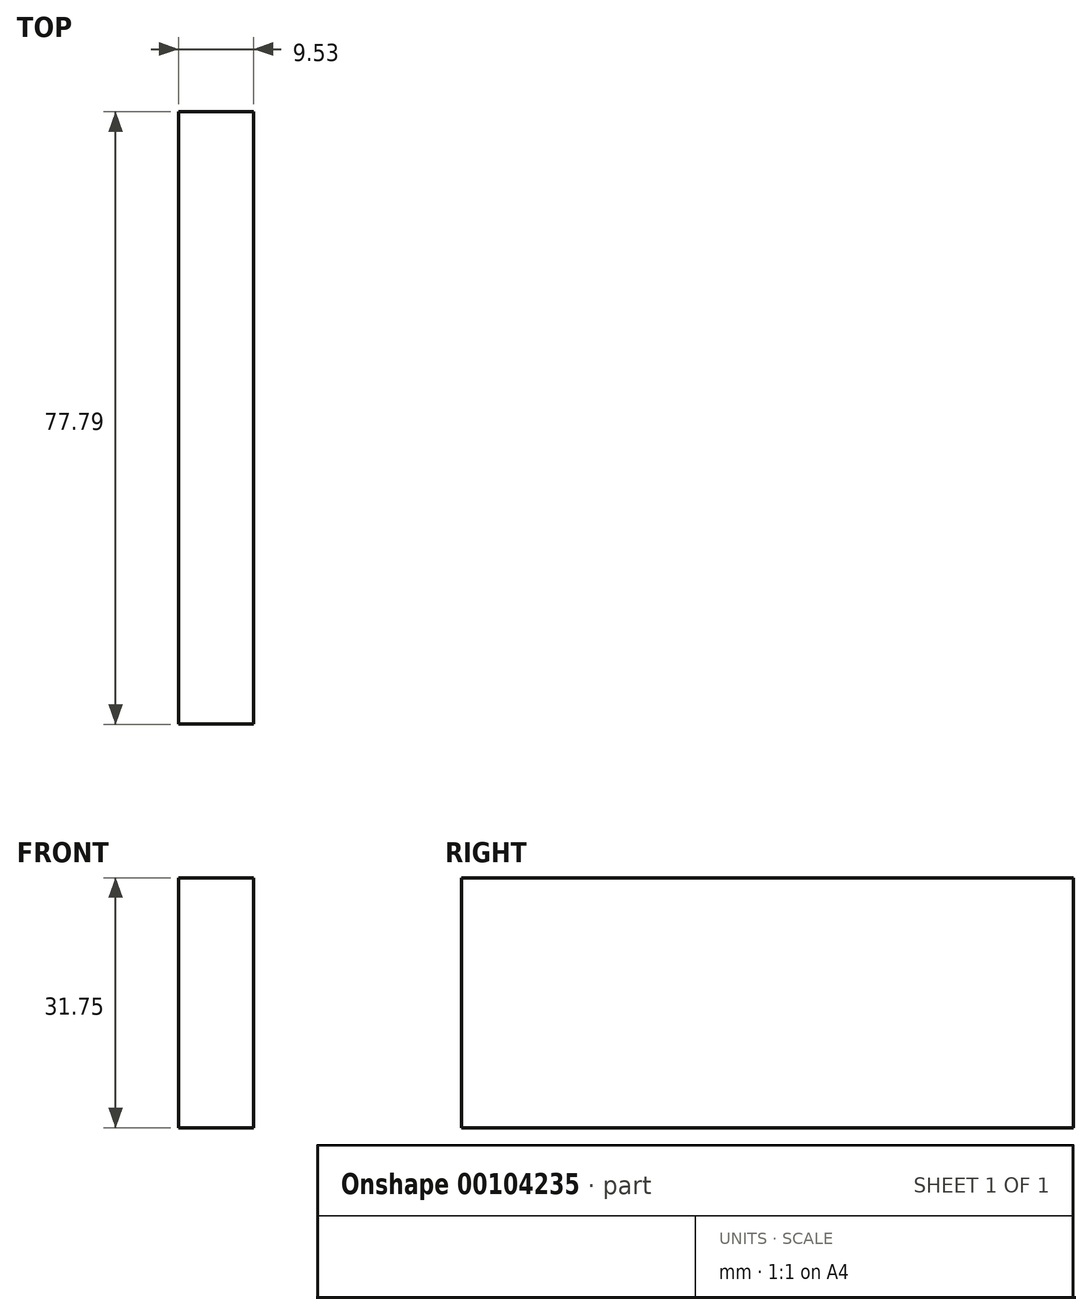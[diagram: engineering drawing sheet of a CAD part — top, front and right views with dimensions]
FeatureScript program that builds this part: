
annotation { "Feature Type Name" : "Feature", "Feature Type Description" : "" }
export const myFeature = defineFeature(function(context is Context, id is Id, definition is map)
    precondition{}
    {
        {
            var Q0;
            Q0=qCreatedBy(makeId("Front.planeOp"),FACE);
            var sketch = newSketch(context, id + "F0", { "sketchPlane" : qUnion([Q0])});
            skLineSegment(sketch, "E0.bottom", {"start": v(-32.14, 18.6) * mm, "end": v(-22.61, 18.6) * mm});
            skLineSegment(sketch, "E0.top", {"start": v(-32.14, -13.15) * mm, "end": v(-22.61, -13.15) * mm});
            skLineSegment(sketch, "E0.left", {"start": v(-32.14, 18.6) * mm, "end": v(-32.14, -13.15) * mm});
            skLineSegment(sketch, "E0.right", {"start": v(-22.61, 18.6) * mm, "end": v(-22.61, -13.15) * mm});
            skSolve(sketch);
        }
        {
            var Q0;
            Q0=makeQuery(id+"F0.imprint","IMPRINT",FACE,{"disambiguationData":[TD([[makeQuery(id+"F0.imprint","IMPRINT",EDGE,{"derivedFrom":sQuery(id+"F0.wireOp",EDGE,"E0.bottom")}),-1.0]])]});
            extrude(context, id + "F1", {"entities" : qUnion([Q0]), "depth" : 77.8 * mm});
        }
    });
